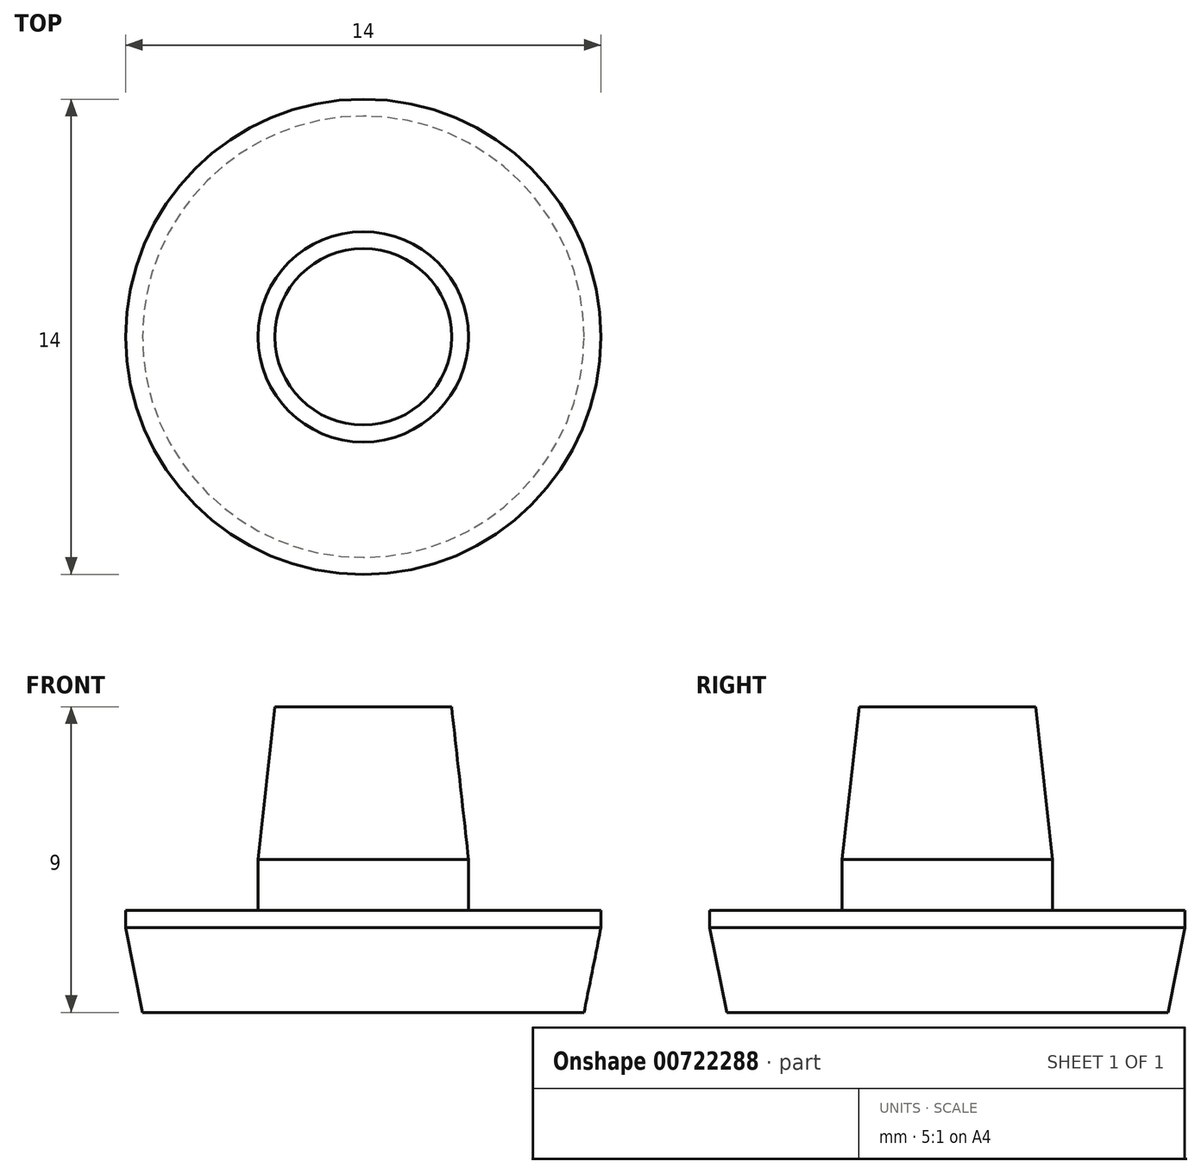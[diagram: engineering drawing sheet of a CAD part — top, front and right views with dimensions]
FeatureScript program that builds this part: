
annotation { "Feature Type Name" : "Feature", "Feature Type Description" : "" }
export const myFeature = defineFeature(function(context is Context, id is Id, definition is map)
    precondition{}
    {
        {
            var Q0;
            Q0=qCreatedBy(makeId("Top.planeOp"),FACE);
            var sketch = newSketch(context, id + "F0", { "sketchPlane" : qUnion([Q0])});
            skCircle(sketch, "E0", {"center": v(0, 0) * mm, "radius": 7 * mm});
            skSolve(sketch);
        }
        {
            var Q0;
            Q0=makeQuery(id+"F0.imprint","IMPRINT",FACE,{"disambiguationData":[TD([[makeQuery(id+"F0.imprint","IMPRINT",EDGE,{"derivedFrom":sQuery(id+"F0.wireOp",EDGE,"E0")}),1.0]])]});
            extrude(context, id + "F1", {"entities" : qUnion([Q0]), "depth" : 3 * mm, "offsetDistance" : 25 * mm});
        }
        {
            var Q0;
            Q0=makeQuery(id+"F1.opExtrude","CAP_FACE",FACE,{"disambiguationData":[OSD([sQuery(id+"F0.wireOp",EDGE,"E0")])],"isStart":false});
            var sketch = newSketch(context, id + "F2", { "sketchPlane" : qUnion([Q0])});
            skCircle(sketch, "E1", {"center": v(0, 0) * mm, "radius": 3.1 * mm});
            skSolve(sketch);
        }
        {
            var Q0;
            Q0=makeQuery(id+"F2.imprint","IMPRINT",FACE,{"disambiguationData":[TD([[makeQuery(id+"F2.imprint","IMPRINT",EDGE,{"derivedFrom":sQuery(id+"F2.wireOp",EDGE,"E1")}),1.0]])]});
            extrude(context, id + "F3", {"entities" : qUnion([Q0]), "operationType" : NewBodyOperationType.ADD, "depth" : 6 * mm, "offsetDistance" : 25 * mm});
        }
        {
            var Q0;
            Q0=makeQuery(id+"F3.opExtrude","CAP_EDGE",EDGE,{"disambiguationData":[OSD([sQuery(id+"F2.wireOp",EDGE,"E1")])],"isStart":false});
            chamfer(context, id + "F4", {"entities" : qUnion([Q0]), "chamferType" : ChamferType.TWO_OFFSETS, "width1" : 0.5 * mm, "oppositeDirection" : false, "width2" : 4.5 * mm, "tangentPropagation" : true});
        }
        {
            var Q0;
            Q0=makeQuery(id+"F1.opExtrude","CAP_EDGE",EDGE,{"disambiguationData":[OSD([sQuery(id+"F0.wireOp",EDGE,"E0")])],"isStart":true});
            chamfer(context, id + "F5", {"entities" : qUnion([Q0]), "chamferType" : ChamferType.TWO_OFFSETS, "width1" : 2.5 * mm, "oppositeDirection" : false, "width2" : 0.5 * mm, "tangentPropagation" : true});
        }
    });
